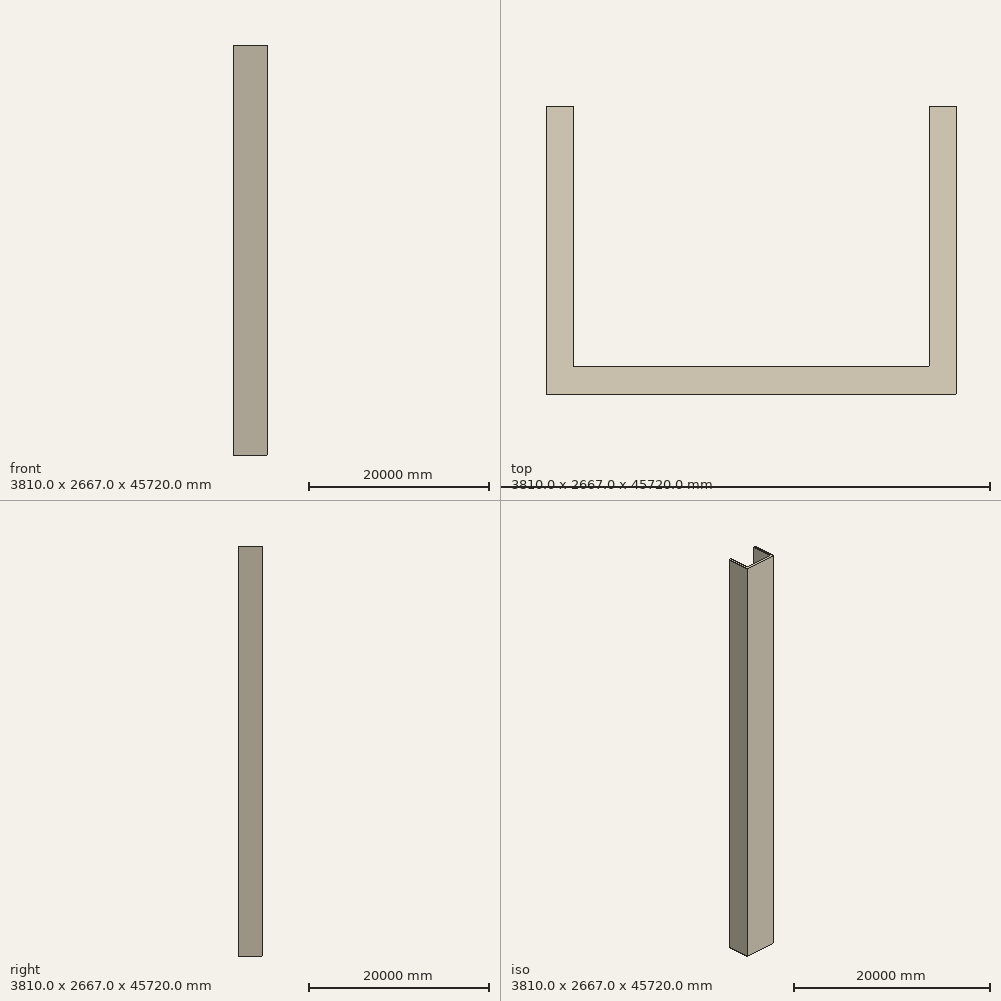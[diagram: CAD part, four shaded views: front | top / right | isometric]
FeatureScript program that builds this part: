
annotation { "Feature Type Name" : "Feature", "Feature Type Description" : "" }
export const myFeature = defineFeature(function(context is Context, id is Id, definition is map)
    precondition{}
    {
        {
            var Q0;
            Q0=qCreatedBy(makeId("Top.planeOp"),FACE);
            var sketch = newSketch(context, id + "F0", { "sketchPlane" : qUnion([Q0])});
            skLineSegment(sketch, "E0", {"start": v(-1905, 0) * mm, "end": v(1905, 0) * mm});
            skLineSegment(sketch, "E1", {"start": v(1905, 0) * mm, "end": v(1905, 2667) * mm});
            skLineSegment(sketch, "E2", {"start": v(1905, 2667) * mm, "end": v(1651, 2667) * mm});
            skLineSegment(sketch, "E3", {"start": v(1651, 2667) * mm, "end": v(1651, 254) * mm});
            skLineSegment(sketch, "E4", {"start": v(1651, 254) * mm, "end": v(-1651, 254) * mm});
            skLineSegment(sketch, "E5", {"start": v(-1651, 254) * mm, "end": v(-1651, 2667) * mm});
            skLineSegment(sketch, "E6", {"start": v(-1651, 2667) * mm, "end": v(-1905, 2667) * mm});
            skLineSegment(sketch, "E7", {"start": v(-1905, 2667) * mm, "end": v(-1905, 0) * mm});
            skSolve(sketch);
        }
        {
            var Q0;
            Q0=makeQuery(id+"F0.imprint","IMPRINT",FACE,{"disambiguationData":[TD([[makeQuery(id+"F0.imprint","IMPRINT",EDGE,{"derivedFrom":sQuery(id+"F0.wireOp",EDGE,"E0")}),1.0]])]});
            extrude(context, id + "F1", {"entities" : qUnion([Q0]), "endBound" : BoundingType.SYMMETRIC, "depth" : 45720 * mm});
        }
    });
